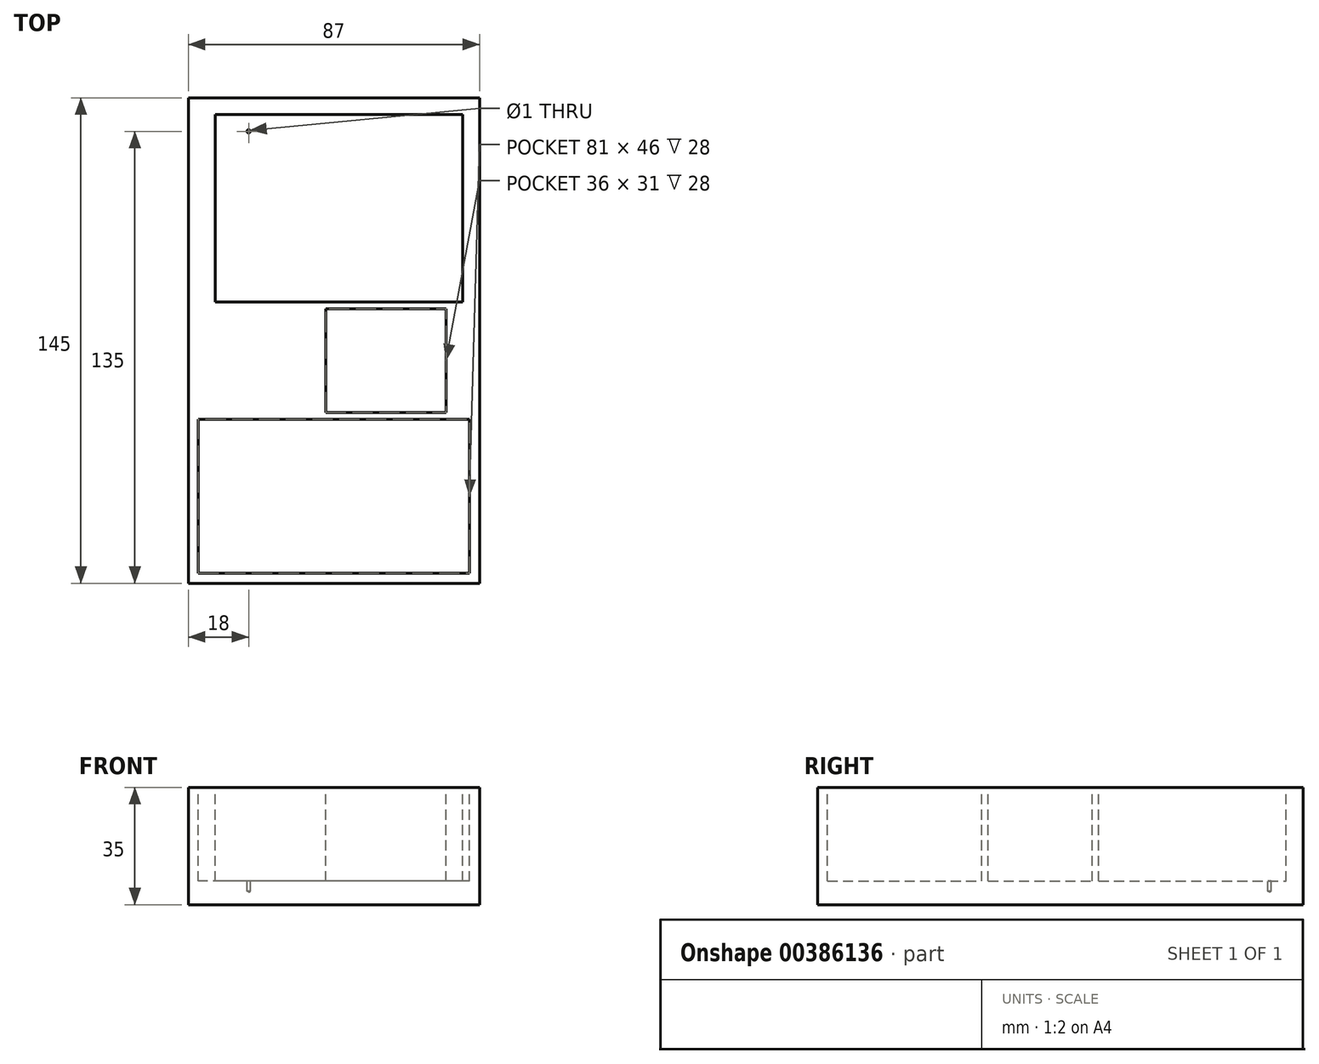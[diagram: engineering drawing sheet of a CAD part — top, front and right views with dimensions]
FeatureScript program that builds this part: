
annotation { "Feature Type Name" : "Feature", "Feature Type Description" : "" }
export const myFeature = defineFeature(function(context is Context, id is Id, definition is map)
    precondition{}
    {
        {
            var Q0;
            Q0=qCreatedBy(makeId("Top.planeOp"),FACE);
            var sketch = newSketch(context, id + "F0", { "sketchPlane" : qUnion([Q0])});
            skLineSegment(sketch, "E0.bottom", {"start": v(43.5, -72.5) * mm, "end": v(-43.5, -72.5) * mm});
            skLineSegment(sketch, "E0.top", {"start": v(43.5, 72.5) * mm, "end": v(-43.5, 72.5) * mm});
            skLineSegment(sketch, "E0.left", {"start": v(43.5, -72.5) * mm, "end": v(43.5, 72.5) * mm});
            skLineSegment(sketch, "E0.right", {"start": v(-43.5, -72.5) * mm, "end": v(-43.5, 72.5) * mm});
            skPoint(sketch, "E0.middle", {"position": v(0, 0) * mm});
            skSolve(sketch);
        }
        {
            var Q0;
            Q0=makeQuery(id+"F0.imprint","IMPRINT",FACE,{"disambiguationData":[TD([[makeQuery(id+"F0.imprint","IMPRINT",EDGE,{"derivedFrom":sQuery(id+"F0.wireOp",EDGE,"E0.bottom")}),-1.0]])]});
            extrude(context, id + "F1", {"entities" : qUnion([Q0]), "depth" : 35 * mm});
        }
        {
            var Q0;
            Q0=makeQuery(id+"F1.opExtrude","CAP_FACE",FACE,{"disambiguationData":[OSD([sQuery(id+"F0.wireOp",EDGE,"E0.bottom"),sQuery(id+"F0.wireOp",EDGE,"E0.top"),sQuery(id+"F0.wireOp",EDGE,"E0.left"),sQuery(id+"F0.wireOp",EDGE,"E0.right")])],"isStart":false});
            var sketch = newSketch(context, id + "F2", { "sketchPlane" : qUnion([Q0])});
            skLineSegment(sketch, "E1.bottom", {"start": v(40.5, -69.5) * mm, "end": v(-40.5, -69.5) * mm});
            skLineSegment(sketch, "E1.top", {"start": v(40.5, -23.5) * mm, "end": v(-40.5, -23.5) * mm});
            skLineSegment(sketch, "E1.left", {"start": v(40.5, -69.5) * mm, "end": v(40.5, -23.5) * mm});
            skLineSegment(sketch, "E1.right", {"start": v(-40.5, -69.5) * mm, "end": v(-40.5, -23.5) * mm});
            skPoint(sketch, "E1.middle", {"position": v(0, -46.5) * mm});
            skLineSegment(sketch, "E2.bottom", {"start": v(33.5, -21.5) * mm, "end": v(-2.5, -21.5) * mm});
            skLineSegment(sketch, "E2.top", {"start": v(33.5, 9.5) * mm, "end": v(-2.5, 9.5) * mm});
            skLineSegment(sketch, "E2.left", {"start": v(33.5, -21.5) * mm, "end": v(33.5, 9.5) * mm});
            skLineSegment(sketch, "E2.right", {"start": v(-2.5, -21.5) * mm, "end": v(-2.5, 9.5) * mm});
            skPoint(sketch, "E2.middle", {"position": v(15.5, -6) * mm});
            skLineSegment(sketch, "E3.bottom", {"start": v(38.5, 11.5) * mm, "end": v(-35.5, 11.5) * mm});
            skLineSegment(sketch, "E3.top", {"start": v(38.5, 67.5) * mm, "end": v(-35.5, 67.5) * mm});
            skLineSegment(sketch, "E3.left", {"start": v(38.5, 11.5) * mm, "end": v(38.5, 67.5) * mm});
            skLineSegment(sketch, "E3.right", {"start": v(-35.5, 11.5) * mm, "end": v(-35.5, 67.5) * mm});
            skPoint(sketch, "E3.middle", {"position": v(1.5, 39.5) * mm});
            skPoint(sketch, "E4", {"position": v(-25.5, 62.5) * mm});
            skSolve(sketch);
        }
        {
            var Q0;
            Q0=makeQuery(id+"F2.imprint","IMPRINT",FACE,{"disambiguationData":[TD([[makeQuery(id+"F2.imprint","IMPRINT",EDGE,{"derivedFrom":sQuery(id+"F2.wireOp",EDGE,"E3.bottom")}),-1.0]])]});
            var Q1;
            Q1=makeQuery(id+"F2.imprint","IMPRINT",FACE,{"disambiguationData":[TD([[makeQuery(id+"F2.imprint","IMPRINT",EDGE,{"derivedFrom":sQuery(id+"F2.wireOp",EDGE,"E2.bottom")}),-1.0]])]});
            var Q2;
            Q2=makeQuery(id+"F2.imprint","IMPRINT",FACE,{"disambiguationData":[TD([[makeQuery(id+"F2.imprint","IMPRINT",EDGE,{"derivedFrom":sQuery(id+"F2.wireOp",EDGE,"E1.bottom")}),-1.0]])]});
            extrude(context, id + "F3", {"entities" : qUnion([Q0, Q1, Q2]), "operationType" : NewBodyOperationType.REMOVE, "oppositeDirection" : true, "depth" : 28 * mm});
        }
        {
            var Q0;
            Q0=sQuery(id+"F2.wireOp",VERTEX,"E4");
            var Q1;
            Q1=makeQuery(id+"F1.opExtrude","SWEPT_BODY",BODY,{"disambiguationData":[OSD([sQuery(id+"F0.wireOp",EDGE,"E0.bottom"),sQuery(id+"F0.wireOp",EDGE,"E0.top"),sQuery(id+"F0.wireOp",EDGE,"E0.left"),sQuery(id+"F0.wireOp",EDGE,"E0.right")])]});
            hole(context, id + "F4", {"style" : HoleStyle.SIMPLE, "endStyle" : HoleEndStyle.BLIND, "holeDiameter" : 1 * mm, "holeDepth" : 3 * mm, "isTappedThrough" : true, "tappedDepth" : 12 * mm, "tapClearance" : 3, "locations" : qUnion([Q0]), "scope" : qUnion([Q1])});
        }
    });
